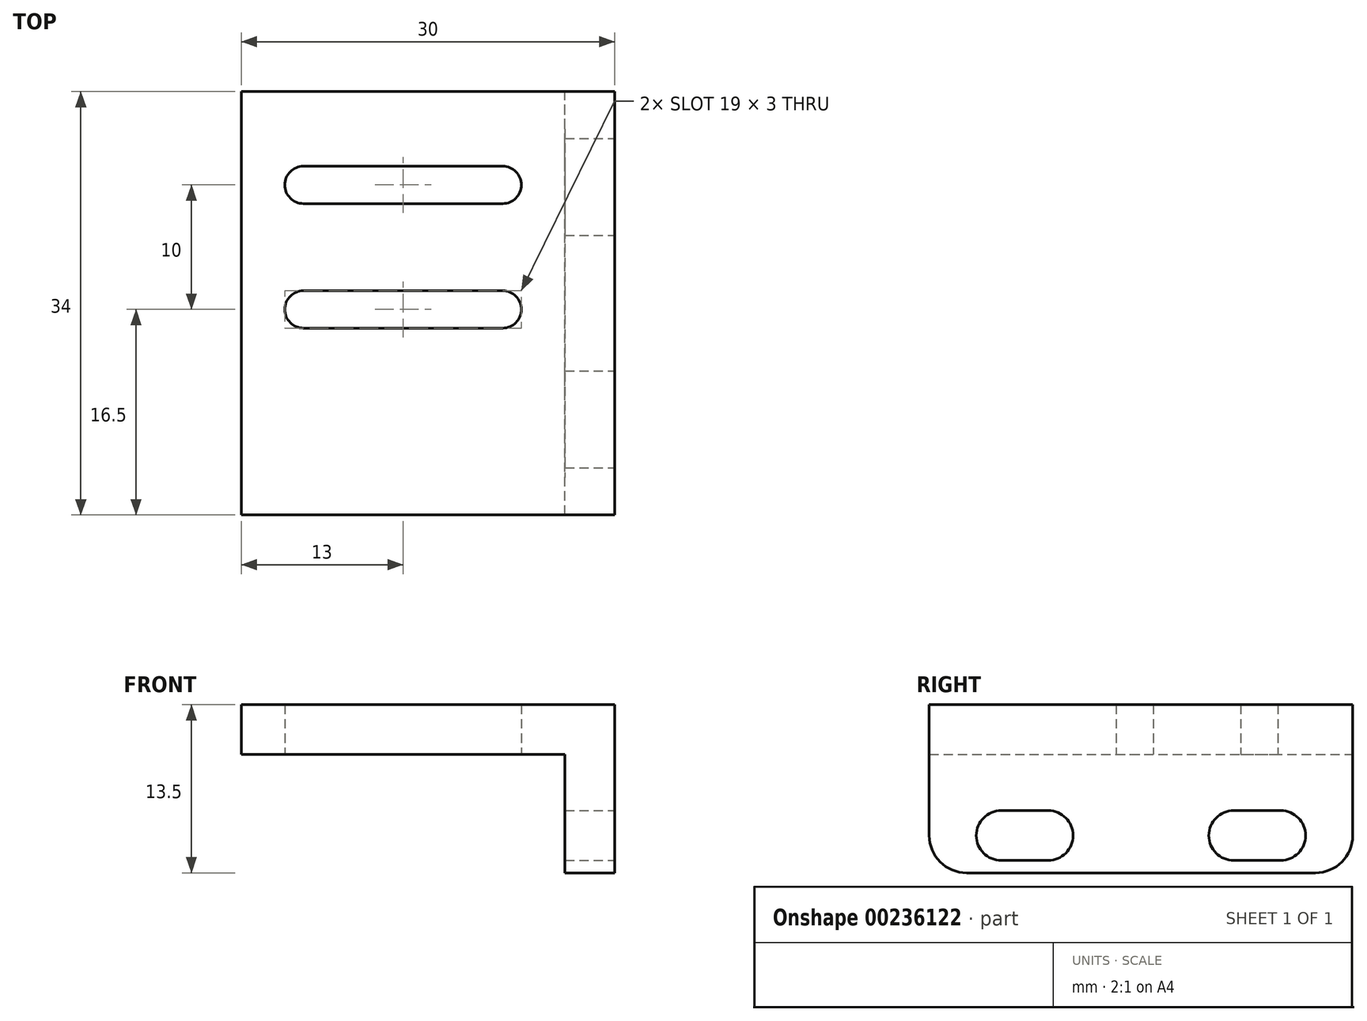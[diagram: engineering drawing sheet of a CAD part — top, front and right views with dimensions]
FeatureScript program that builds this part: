
annotation { "Feature Type Name" : "Feature", "Feature Type Description" : "" }
export const myFeature = defineFeature(function(context is Context, id is Id, definition is map)
    precondition{}
    {
        {
            var Q0;
            Q0=qCreatedBy(makeId("Right.planeOp"),FACE);
            var sketch = newSketch(context, id + "F0", { "sketchPlane" : qUnion([Q0])});
            skLineSegment(sketch, "E0.0", {"start": v(0, 32.55) * mm, "end": v(28, 32.55) * mm});
            skArc(sketch, "E0.1", {"start": v(0, 32.55) * mm, "mid": v(-2.12, 31.67) * mm, "end": v(-3, 29.55) * mm});
            skLineSegment(sketch, "E0.2", {"start": v(28, 26.55) * mm, "end": v(0, 26.55) * mm});
            skArc(sketch, "E0.3", {"start": v(28, 26.55) * mm, "mid": v(30.12, 27.43) * mm, "end": v(31, 29.55) * mm});
            skLineSegment(sketch, "E1", {"start": v(0, 29.55) * mm, "end": v(-10.51, 29.55) * mm, "construction": true});
            skPoint(sketch, "E1.endSnap0", {"position": v(-2, 29.55) * mm});
            skArc(sketch, "E2", {"start": v(-3, 29.55) * mm, "mid": v(-2.12, 27.43) * mm, "end": v(0, 26.55) * mm});
            skPoint(sketch, "E3.endSnap0", {"position": v(31, 29.55) * mm});
            skArc(sketch, "E4", {"start": v(31, 29.55) * mm, "mid": v(30.12, 31.67) * mm, "end": v(28, 32.55) * mm});
            skLineSegment(sketch, "E5", {"start": v(-3, 29.55) * mm, "end": v(-3, 36.05) * mm});
            skLineSegment(sketch, "E6", {"start": v(31, 36.05) * mm, "end": v(31, 29.55) * mm});
            skLineSegment(sketch, "E7.bottom", {"start": v(-3, 36.05) * mm, "end": v(31, 36.05) * mm});
            skLineSegment(sketch, "E8", {"start": v(-3, 29.55) * mm, "end": v(31, 29.55) * mm, "construction": true});
            skLineSegment(sketch, "E9", {"start": v(14, 29.55) * mm, "end": v(14, 38.96) * mm, "construction": true});
            skArc(sketch, "E10", {"start": v(2.78, 31.55) * mm, "mid": v(0.78, 29.55) * mm, "end": v(2.78, 27.55) * mm});
            skLineSegment(sketch, "E11", {"start": v(4.66, 31.55) * mm, "end": v(4.66, 27.55) * mm, "construction": true});
            skArc(sketch, "E12.MirrorCS", {"start": v(6.55, 31.55) * mm, "mid": v(8.55, 29.55) * mm, "end": v(6.55, 27.55) * mm});
            skLineSegment(sketch, "E13", {"start": v(2.78, 31.55) * mm, "end": v(6.55, 31.55) * mm});
            skLineSegment(sketch, "E14", {"start": v(6.55, 27.55) * mm, "end": v(2.78, 27.55) * mm});
            skLineSegment(sketch, "E15.MirrorCS", {"start": v(6.55, 31.55) * mm, "end": v(2.78, 31.55) * mm});
            skLineSegment(sketch, "E16.MirrorCS", {"start": v(2.78, 27.55) * mm, "end": v(6.55, 27.55) * mm});
            skLineSegment(sketch, "E17.MirrorCS", {"start": v(25.22, 31.55) * mm, "end": v(21.45, 31.55) * mm});
            skArc(sketch, "E18.MirrorCS", {"start": v(21.45, 31.55) * mm, "mid": v(19.45, 29.55) * mm, "end": v(21.45, 27.55) * mm});
            skLineSegment(sketch, "E19.MirrorCS", {"start": v(25.22, 27.55) * mm, "end": v(21.45, 27.55) * mm});
            skLineSegment(sketch, "E20.MirrorCS", {"start": v(21.45, 31.55) * mm, "end": v(25.22, 31.55) * mm});
            skLineSegment(sketch, "E21.MirrorCS", {"start": v(23.34, 31.55) * mm, "end": v(23.34, 27.55) * mm, "construction": true});
            skLineSegment(sketch, "E22.MirrorCS", {"start": v(21.45, 27.55) * mm, "end": v(25.22, 27.55) * mm});
            skArc(sketch, "E23.MirrorCS", {"start": v(25.22, 31.55) * mm, "mid": v(27.22, 29.55) * mm, "end": v(25.22, 27.55) * mm});
            skSolve(sketch);
        }
        {
            var Q0;
            Q0=makeQuery(id+"F0.imprint","IMPRINT",FACE,{"disambiguationData":[TD([[makeQuery(id+"F0.imprint","IMPRINT",EDGE,{"derivedFrom":sQuery(id+"F0.wireOp",EDGE,"E0.0")}),1.0]])]});
            var Q1;
            {var subQ0=sQuery(id+"F0.wireOp",EDGE,"r05qNPXO-aBil-uF2h-enEl-UfvkTS2mg0ns");Q1=makeQuery(id+"F0.imprint","IMPRINT",FACE,{"disambiguationData":[TD([[makeQuery(id+"F0.imprint","IMPRINT",EDGE,{"derivedFrom":subQ0}),1.0]])]});}
            var Q2;
            Q2=makeQuery(id+"F0.imprint","IMPRINT",FACE,{"disambiguationData":[TD([[makeQuery(id+"F0.imprint","IMPRINT",EDGE,{"derivedFrom":sQuery(id+"F0.wireOp",EDGE,"E7.bottom")}),1.0]])]});
            var Q3;
            {var subQ0=sQuery(id+"F0.wireOp",EDGE,"a1a1709d-6670-4851-9314-8bf02d63e1fc");Q3=makeQuery(id+"F0.imprint","IMPRINT",FACE,{"disambiguationData":[TD([[makeQuery(id+"F0.imprint","IMPRINT",EDGE,{"derivedFrom":subQ0}),-1.0]])]});}
            var Q4;
            Q4=makeQuery(id+"F0.imprint","IMPRINT",FACE,{"disambiguationData":[TD([[makeQuery(id+"F0.imprint","IMPRINT",EDGE,{"derivedFrom":sQuery(id+"F0.wireOp",EDGE,"E0.0")}),-1.0]])]});
            extrude(context, id + "F1", {"entities" : qUnion([Q0, Q1, Q2, Q3, Q4]), "oppositeDirection" : true, "depth" : 4 * mm});
        }
        {
            var Q0;
            Q0=makeQuery(id+"F1.opExtrude","SWEPT_FACE",FACE,{"disambiguationData":[OSD([sQuery(id+"F0.wireOp",EDGE,"E7.bottom")])]});
            var sketch = newSketch(context, id + "F2", { "sketchPlane" : qUnion([Q0])});
            skLineSegment(sketch, "E24.0", {"start": v(0, -3) * mm, "end": v(0, 31) * mm});
            skPoint(sketch, "E25.oppositeSnap0", {"position": v(-2, 31) * mm});
            skLineSegment(sketch, "E25.bottom", {"start": v(0, -3) * mm, "end": v(-30, -3) * mm});
            skLineSegment(sketch, "E25.top", {"start": v(0, 31) * mm, "end": v(-30, 31) * mm});
            skLineSegment(sketch, "E25.right", {"start": v(-30, -3) * mm, "end": v(-30, 31) * mm});
            skLineSegment(sketch, "E26", {"start": v(-9, 22) * mm, "end": v(-25, 22) * mm});
            skLineSegment(sketch, "E27", {"start": v(-25, 25) * mm, "end": v(-9, 25) * mm});
            skArc(sketch, "E28", {"start": v(-9, 22) * mm, "mid": v(-7.5, 23.5) * mm, "end": v(-9, 25) * mm});
            skArc(sketch, "E29", {"start": v(-9, 25) * mm, "mid": v(-10.5, 23.5) * mm, "end": v(-9, 22) * mm});
            skArc(sketch, "E30", {"start": v(-25, 22) * mm, "mid": v(-23.5, 23.5) * mm, "end": v(-25, 25) * mm});
            skArc(sketch, "E31", {"start": v(-25, 25) * mm, "mid": v(-26.5, 23.5) * mm, "end": v(-25, 22) * mm});
            skLineSegment(sketch, "E32", {"start": v(-9, 12) * mm, "end": v(-25, 12) * mm});
            skLineSegment(sketch, "E33", {"start": v(-25, 15) * mm, "end": v(-9, 15) * mm});
            skArc(sketch, "E34", {"start": v(-9, 12) * mm, "mid": v(-7.5, 13.5) * mm, "end": v(-9, 15) * mm});
            skArc(sketch, "E35", {"start": v(-9, 15) * mm, "mid": v(-10.5, 13.5) * mm, "end": v(-9, 12) * mm});
            skArc(sketch, "E36", {"start": v(-25, 12) * mm, "mid": v(-23.5, 13.5) * mm, "end": v(-25, 15) * mm});
            skArc(sketch, "E37", {"start": v(-25, 15) * mm, "mid": v(-26.5, 13.5) * mm, "end": v(-25, 12) * mm});
            skSolve(sketch);
        }
        {
            var Q0;
            {var subQ0=sQuery(id+"F2.wireOp",EDGE,"E24.0");Q0=makeQuery(id+"F2.imprint","IMPRINT",FACE,{"disambiguationData":[TD([[makeQuery(id+"F2.imprint","IMPRINT",EDGE,{"derivedFrom":subQ0}),1.0]])]});}
            var Q1;
            {var subQ0=sQuery(id+"F2.wireOp",EDGE,"E25.right");Q1=makeQuery(id+"F2.imprint","IMPRINT",FACE,{"disambiguationData":[TD([[makeQuery(id+"F2.imprint","IMPRINT",EDGE,{"derivedFrom":subQ0}),-1.0]])]});}
            extrude(context, id + "F3", {"entities" : qUnion([Q0, Q1]), "operationType" : NewBodyOperationType.ADD, "depth" : 4 * mm});
        }
    });
